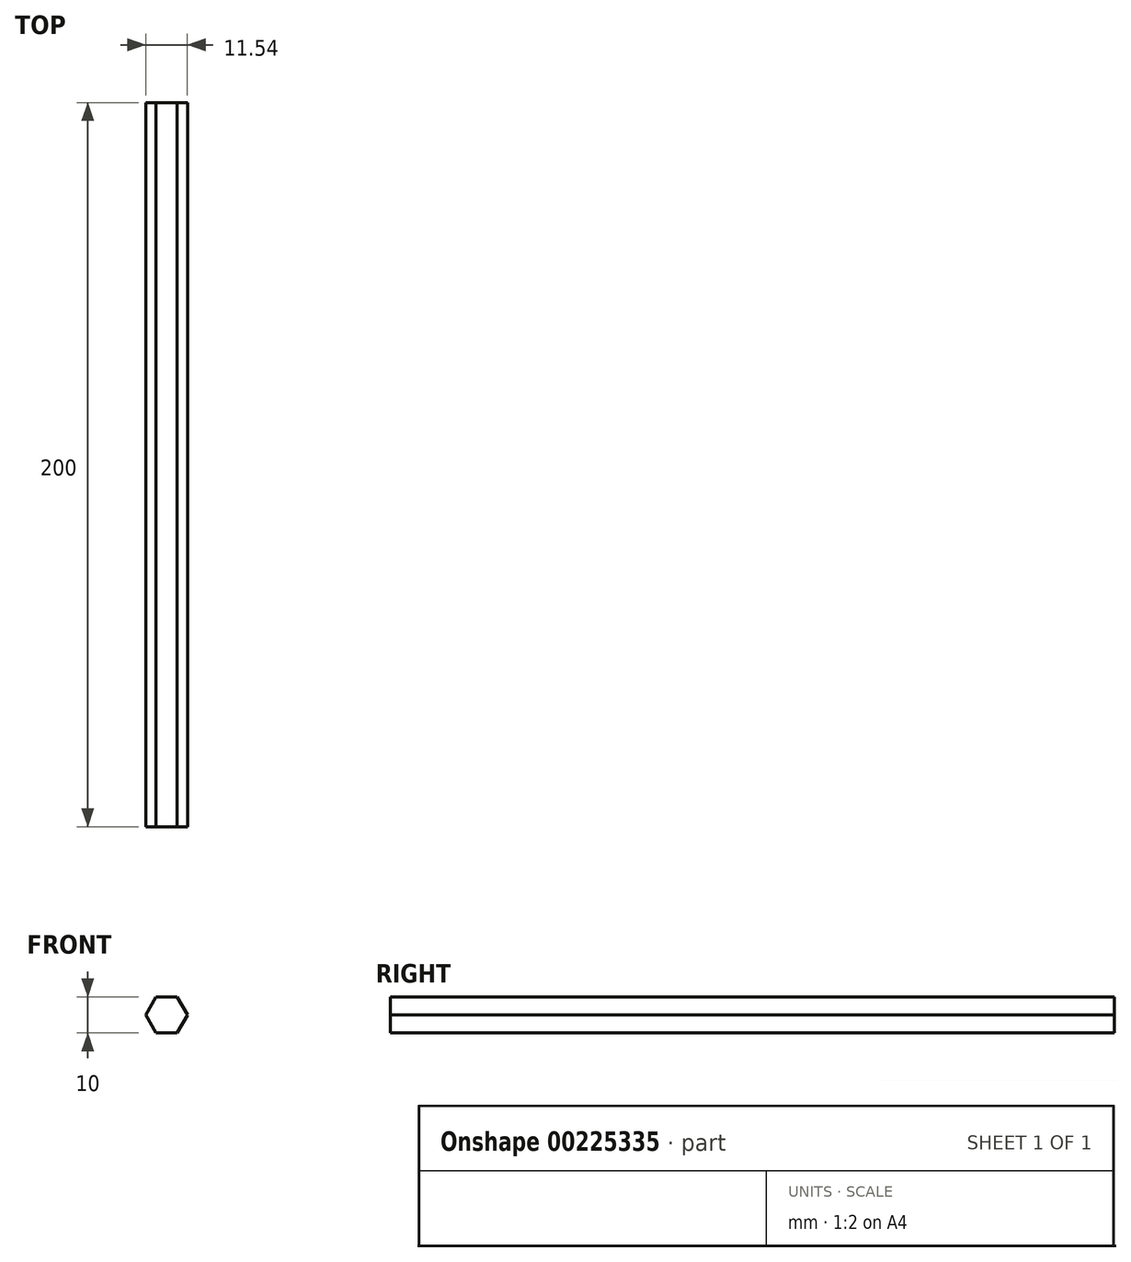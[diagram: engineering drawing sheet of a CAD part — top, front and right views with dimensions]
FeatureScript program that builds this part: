
annotation { "Feature Type Name" : "Feature", "Feature Type Description" : "" }
export const myFeature = defineFeature(function(context is Context, id is Id, definition is map)
    precondition{}
    {
        {
            var Q0;
            Q0=qCreatedBy(makeId("Front.planeOp"),FACE);
            var sketch = newSketch(context, id + "F0", { "sketchPlane" : qUnion([Q0])});
            skCircle(sketch, "E0.cCircle", {"center": v(0, 0) * mm, "radius": 5 * mm, "construction": true});
            skLineSegment(sketch, "E0.0", {"start": v(5.77, 0) * mm, "end": v(2.89, -5) * mm});
            skLineSegment(sketch, "E0.1", {"start": v(2.89, -5) * mm, "end": v(-2.89, -5) * mm});
            skLineSegment(sketch, "E0.2", {"start": v(-2.89, -5) * mm, "end": v(-5.77, 0) * mm});
            skLineSegment(sketch, "E0.3", {"start": v(-5.77, 0) * mm, "end": v(-2.89, 5) * mm});
            skLineSegment(sketch, "E0.4", {"start": v(-2.89, 5) * mm, "end": v(2.89, 5) * mm});
            skLineSegment(sketch, "E0.5", {"start": v(2.89, 5) * mm, "end": v(5.77, 0) * mm});
            skPoint(sketch, "E0.0.midPoint", {"position": v(4.33, -2.5) * mm});
            skSolve(sketch);
        }
        {
            var Q0;
            Q0 = qSketchRegion(id + "F0", true);
            extrude(context, id + "F1", {"entities" : qUnion([Q0]), "depth" : 200 * mm});
        }
    });
